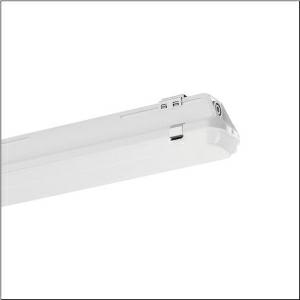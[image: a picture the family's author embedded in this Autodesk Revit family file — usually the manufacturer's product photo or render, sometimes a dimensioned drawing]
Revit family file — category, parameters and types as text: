
# Revit family: monsun_r__21_51fb10dp360b_a0ac
name_source: partatom
category: Lighting Fixtures
units: mm (PartAtom-declared; Revit-internal decimal feet)

## family parameters
Cut with Voids When Loaded = No
Host = Face
Light Source = No
Part Type = Normal
Room Calculation Point = No
Round Connector Dimension = Use Diameter
Shared = No

## types (1)
- --- (1 x LED, 6060 lm, 43.2 W, 3000K)
    Apparent Load = 43 VA
    CIE Flux Codes = 47 77 93 94 100
    Color Rendering = 80
    Color Temperature = 3000K
    Default Elevation = 1800 mm
    Description = Monsun® 21, damp-proof luminaire, chain hanger, primary optical cover: enclosure, of PMMA, light emission: direct distribution, primary light characteristic: symmetric, installation type: suspended mounting, surface-mounted, horizontal mounting, vertical mounting, LED, rated luminous flux: 6.060lm, luminous efficacy: 154lm/W, light colour: 830, colour temperature: 3000K, control gear: DALI 2, with terminal, 5-pole, max. 2.5mm², mains connection: 220..240V, AC, 50/60Hz, rated input power: 39W, housing, of glass-fibre reinforced polyester, uncoated, bright grey, incl. chain hanger, length: 1.590mm, width: 90mm, height: 88mm, clip for enclosure, of stainless steel (V2A), ceiling mounting element, of stainless steel (V2A), chain hanger, of stainless steel (V2A), protection rating (complete): IP66, insulation class (complete): insulation class I (protective earthing), certification: CE, ENEC, VDE, UKCA, protection symbol: D, impact resistance: IK04, permissible operating ambient temperature: -25..+35°C, standard: EN 50419, EN 60598-2-1, corresponds to IFS (International Featured Standards) requirements for safety and quality in the food industry, for indoor or canopied outdoor use, no direct snow, no direct sun, no direct rain, contact your sales advisor before using the luminaires in applications with unclear chemical exposure, large temperature fluctuations or condensation-forming humidity, LABS conformity tested according to VDMA 24364:2018-05, packaging unit: 1 piece
    Height = 89 mm
    Lamp = 1 x LED
    Lamp Light Flux = 6060 lm
    Lamp Power = 43.2 W
    Lamp count = 1
    Length = 1590 mm
    Luminous efficacy = 140 lm/W
    Manufacturer = Siteco
    ModVariant = No
    Model = 51FB10DP360B
    Mounting Place = Ceiling
    Mounting Type = Surface mounted
    Number of Poles = 1
    OnlyDefault = Yes
    Power Factor = 1
    Product Name = Monsun® 21
    Product group = damp-proof luminaire
    ProductGroupID = 301
    Protection Class = Protection class I
    Protection Degree = IP 66
    RLX_Detail_Level = 1
    RLX_Emergency_Light_Flux = 0 lm
    RLX_Emergency_Type = 0
    RLX_Emergency_Type_DB = No
    RlxData = <blob elided: 92325 chars, md5=4230dc85>
    Socket = socket
    Standby Power = 0 W
    System Light Flux = 6060 lm
    System Power = 43 W
    Type Comments = factory setting: luminous flux: 100 % | dim-lin: 254 | 286 mA
    Type Image = l_1319656.jpg
    URL = http://relux.com
    VarID = @adj_168217
    Voltage = 0 V
    Weight = 0.00 kg
    Width = 90 mm

## geometry (parser evidence)
native form markers: Blend x4, Sweep x13
no freeform markers — native parametric forms only
